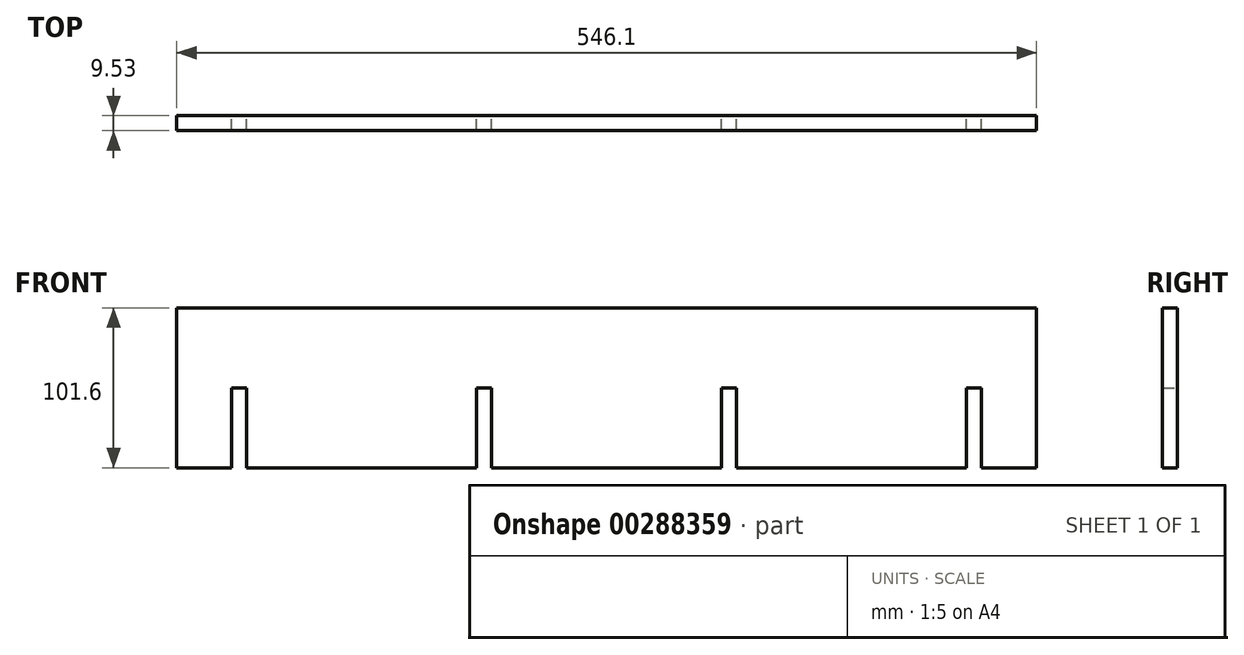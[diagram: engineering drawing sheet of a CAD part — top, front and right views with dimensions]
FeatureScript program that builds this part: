
annotation { "Feature Type Name" : "Feature", "Feature Type Description" : "" }
export const myFeature = defineFeature(function(context is Context, id is Id, definition is map)
    precondition{}
    {
        {
            var Q0;
            Q0=qCreatedBy(makeId("Front.planeOp"),FACE);
            var sketch = newSketch(context, id + "F0", { "sketchPlane" : qUnion([Q0])});
            skLineSegment(sketch, "E0.bottom", {"start": v(-273.05, -50.8) * mm, "end": v(-238.12, -50.8) * mm});
            skLineSegment(sketch, "E0.top", {"start": v(-273.05, 50.8) * mm, "end": v(273.05, 50.8) * mm});
            skLineSegment(sketch, "E0.left", {"start": v(-273.05, -50.8) * mm, "end": v(-273.05, 50.8) * mm});
            skLineSegment(sketch, "E0.right", {"start": v(273.05, -50.8) * mm, "end": v(273.05, 50.8) * mm});
            skPoint(sketch, "E0.middle", {"position": v(0, 0) * mm});
            skPoint(sketch, "E1.oppositeSnap0", {"position": v(-273.05, 0) * mm});
            skLineSegment(sketch, "E1.top", {"start": v(-238.12, 0) * mm, "end": v(-228.6, 0) * mm});
            skLineSegment(sketch, "E1.left", {"start": v(-238.12, -50.8) * mm, "end": v(-238.12, 0) * mm});
            skLineSegment(sketch, "E1.right", {"start": v(-228.6, -50.8) * mm, "end": v(-228.6, 0) * mm});
            skLineSegment(sketch, "E2.trimOffspring", {"start": v(-228.6, -50.8) * mm, "end": v(-82.55, -50.8) * mm});
            skLineSegment(sketch, "E3.top", {"start": v(-82.55, 0) * mm, "end": v(-73.02, 0) * mm});
            skLineSegment(sketch, "E3.left", {"start": v(-82.55, -50.8) * mm, "end": v(-82.55, 0) * mm});
            skLineSegment(sketch, "E3.right", {"start": v(-73.02, -50.8) * mm, "end": v(-73.02, 0) * mm});
            skLineSegment(sketch, "E4.top", {"start": v(73.03, 0) * mm, "end": v(82.55, 0) * mm});
            skLineSegment(sketch, "E4.left", {"start": v(73.03, -50.8) * mm, "end": v(73.03, 0) * mm});
            skLineSegment(sketch, "E4.right", {"start": v(82.55, -50.8) * mm, "end": v(82.55, 0) * mm});
            skLineSegment(sketch, "E5.trimOffspring", {"start": v(-73.02, -50.8) * mm, "end": v(73.03, -50.8) * mm});
            skLineSegment(sketch, "E6.trimOffspring", {"start": v(82.55, -50.8) * mm, "end": v(228.6, -50.8) * mm});
            skLineSegment(sketch, "E7.top", {"start": v(228.6, 0) * mm, "end": v(238.12, 0) * mm});
            skLineSegment(sketch, "E7.left", {"start": v(228.6, -50.8) * mm, "end": v(228.6, 0) * mm});
            skLineSegment(sketch, "E7.right", {"start": v(238.12, -50.8) * mm, "end": v(238.12, 0) * mm});
            skLineSegment(sketch, "E8.trimOffspring", {"start": v(238.13, -50.8) * mm, "end": v(273.05, -50.8) * mm});
            skSolve(sketch);
        }
        {
            var Q0;
            Q0 = qSketchRegion(id + "F0", true);
            extrude(context, id + "F1", {"entities" : qUnion([Q0]), "depth" : 9.52 * mm});
        }
    });
